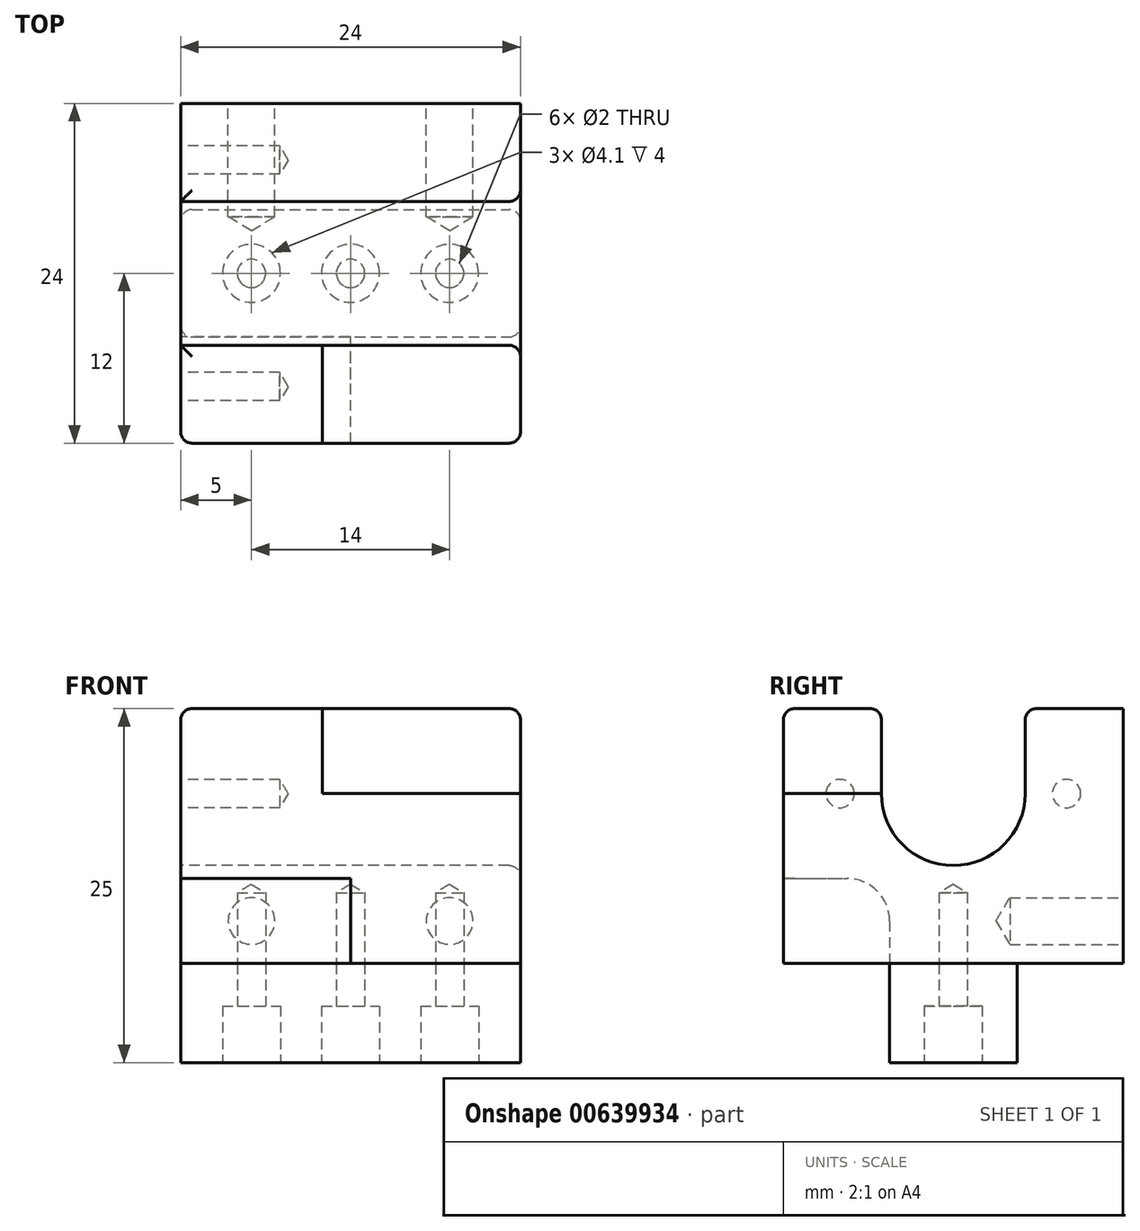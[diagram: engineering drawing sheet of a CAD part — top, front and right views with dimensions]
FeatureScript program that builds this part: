
annotation { "Feature Type Name" : "Feature", "Feature Type Description" : "" }
export const myFeature = defineFeature(function(context is Context, id is Id, definition is map)
    precondition{}
    {
        {
            var Q0;
            Q0=qCreatedBy(makeId("Right.planeOp"),FACE);
            var sketch = newSketch(context, id + "F0", { "sketchPlane" : qUnion([Q0])});
            skLineSegment(sketch, "E0.bottom", {"start": v(0, 0) * mm, "end": v(24, 0) * mm});
            skLineSegment(sketch, "E0.top", {"start": v(0, 18) * mm, "end": v(24, 18) * mm});
            skLineSegment(sketch, "E0.left", {"start": v(0, 0) * mm, "end": v(0, 18) * mm});
            skLineSegment(sketch, "E0.right", {"start": v(24, 0) * mm, "end": v(24, 18) * mm});
            skCircle(sketch, "E1", {"center": v(12, 12) * mm, "radius": 5.08 * mm});
            skLineSegment(sketch, "E2", {"start": v(12, 18) * mm, "end": v(12, 0) * mm, "construction": true});
            skLineSegment(sketch, "E3.bottom", {"start": v(17.08, 12) * mm, "end": v(6.92, 12) * mm});
            skLineSegment(sketch, "E3.top", {"start": v(17.08, 18) * mm, "end": v(6.92, 18) * mm});
            skLineSegment(sketch, "E3.left", {"start": v(17.08, 12) * mm, "end": v(17.08, 18) * mm});
            skLineSegment(sketch, "E3.right", {"start": v(6.92, 12) * mm, "end": v(6.92, 18) * mm});
            skSolve(sketch);
        }
        {
            var Q0;
            Q0=makeQuery(id+"F0.imprint","IMPRINT",FACE,{"disambiguationData":[TD([[makeQuery(id+"F0.imprint","IMPRINT",EDGE,{"derivedFrom":sQuery(id+"F0.wireOp",EDGE,"E0.bottom")}),1.0]])]});
            extrude(context, id + "F1", {"entities" : qUnion([Q0]), "depth" : 24 * mm, "offsetDistance" : 25 * mm});
        }
        {
            var Q0;
            Q0=makeQuery(id+"F1.opExtrude","CAP_FACE",FACE,{"disambiguationData":[OSD([sQuery(id+"F0.wireOp",EDGE,"E0.bottom"),sQuery(id+"F0.wireOp",EDGE,"E0.top"),sQuery(id+"F0.wireOp",EDGE,"E0.left"),sQuery(id+"F0.wireOp",EDGE,"E0.right"),sQuery(id+"F0.wireOp",EDGE,"E1"),sQuery(id+"F0.wireOp",EDGE,"E3.left"),sQuery(id+"F0.wireOp",EDGE,"E3.right")])],"isStart":true});
            var sketch = newSketch(context, id + "F2", { "sketchPlane" : qUnion([Q0])});
            skLineSegment(sketch, "E4", {"start": v(-20, 12) * mm, "end": v(-4, 12) * mm, "construction": true});
            skPoint(sketch, "E5", {"position": v(-20, 12) * mm});
            skPoint(sketch, "E6", {"position": v(-4, 12) * mm});
            skSolve(sketch);
        }
        {
            var Q0;
            Q0=sQuery(id+"F2.wireOp",VERTEX,"E5");
            var Q1;
            Q1=sQuery(id+"F2.wireOp",VERTEX,"E6");
            var Q2;
            Q2=makeQuery(id+"F1.opExtrude","SWEPT_BODY",BODY,{"disambiguationData":[OSD([sQuery(id+"F0.wireOp",EDGE,"E0.bottom"),sQuery(id+"F0.wireOp",EDGE,"E0.top"),sQuery(id+"F0.wireOp",EDGE,"E0.left"),sQuery(id+"F0.wireOp",EDGE,"E0.right"),sQuery(id+"F0.wireOp",EDGE,"E1"),sQuery(id+"F0.wireOp",EDGE,"E3.left"),sQuery(id+"F0.wireOp",EDGE,"E3.right")])]});
            hole(context, id + "F3", {"style" : HoleStyle.SIMPLE, "endStyle" : HoleEndStyle.BLIND, "holeDiameter" : 2 * mm, "majorDiameter" : 5 * mm, "holeDepth" : 7 * mm, "isTappedThrough" : true, "tappedDepth" : 7 * mm, "tapClearance" : 2, "startFromSketch" : true, "locations" : qUnion([Q0, Q1]), "scope" : qUnion([Q2])});
        }
        {
            var Q0;
            Q0=makeQuery(id+"F1.opExtrude","SWEPT_FACE",FACE,{"disambiguationData":[OSD([sQuery(id+"F0.wireOp",EDGE,"E0.right")])]});
            var sketch = newSketch(context, id + "F4", { "sketchPlane" : qUnion([Q0])});
            skLineSegment(sketch, "E7", {"start": v(0, 3) * mm, "end": v(-26.79, 3) * mm, "construction": true});
            skPoint(sketch, "E8", {"position": v(-19, 3) * mm});
            skPoint(sketch, "E9", {"position": v(-5, 3) * mm});
            skSolve(sketch);
        }
        {
            var Q0;
            Q0=sQuery(id+"F4.wireOp",VERTEX,"E8");
            var Q1;
            Q1=sQuery(id+"F4.wireOp",VERTEX,"E9");
            var Q2;
            Q2=makeQuery(id+"F1.opExtrude","SWEPT_BODY",BODY,{"disambiguationData":[OSD([sQuery(id+"F0.wireOp",EDGE,"E0.bottom"),sQuery(id+"F0.wireOp",EDGE,"E0.top"),sQuery(id+"F0.wireOp",EDGE,"E0.left"),sQuery(id+"F0.wireOp",EDGE,"E0.right"),sQuery(id+"F0.wireOp",EDGE,"E1"),sQuery(id+"F0.wireOp",EDGE,"E3.left"),sQuery(id+"F0.wireOp",EDGE,"E3.right")])]});
            hole(context, id + "F5", {"style" : HoleStyle.SIMPLE, "endStyle" : HoleEndStyle.BLIND, "standardTappedOrClearance" : lookupTablePath({ "standard" : "ISO", "fit" : "Normal", "size" : "M3", "type" : "Clearance" }), "standardBlindInLast" : lookupTablePath({ "fit" : "Standard", "standard" : "ISO", "size" : "M3", "type" : "Clearance" }), "holeDiameter" : 3.3 * mm, "majorDiameter" : 5 * mm, "holeDepth" : 8 * mm, "isTappedThrough" : true, "tappedDepth" : 7 * mm, "tapClearance" : 2, "startFromSketch" : true, "locations" : qUnion([Q0, Q1]), "scope" : qUnion([Q2])});
        }
        {
            var Q0;
            Q0=makeQuery(id+"F1.opExtrude","SWEPT_FACE",FACE,{"disambiguationData":[OSD([sQuery(id+"F0.wireOp",EDGE,"E0.bottom")])]});
            var sketch = newSketch(context, id + "F6", { "sketchPlane" : qUnion([Q0])});
            skLineSegment(sketch, "E10.bottom", {"start": v(0, -7.5) * mm, "end": v(24, -7.5) * mm});
            skLineSegment(sketch, "E10.top", {"start": v(0, -16.5) * mm, "end": v(24, -16.5) * mm});
            skLineSegment(sketch, "E10.left", {"start": v(0, -7.5) * mm, "end": v(0, -16.5) * mm});
            skLineSegment(sketch, "E10.right", {"start": v(24, -7.5) * mm, "end": v(24, -16.5) * mm});
            skSolve(sketch);
        }
        {
            var Q0;
            Q0 = qSketchRegion(id + "F6", true);
            extrude(context, id + "F7", {"entities" : qUnion([Q0]), "depth" : 7 * mm, "offsetDistance" : 25 * mm});
        }
        {
            var Q0;
            Q0=makeQuery(id+"F7.opExtrude","CAP_FACE",FACE,{"disambiguationData":[OSD([sQuery(id+"F6.wireOp",EDGE,"E10.bottom"),sQuery(id+"F6.wireOp",EDGE,"E10.top"),sQuery(id+"F6.wireOp",EDGE,"E10.left"),sQuery(id+"F6.wireOp",EDGE,"E10.right")])],"isStart":false});
            var sketch = newSketch(context, id + "F8", { "sketchPlane" : qUnion([Q0])});
            skLineSegment(sketch, "E11", {"start": v(24, -12) * mm, "end": v(0, -12) * mm, "construction": true});
            skPoint(sketch, "E12", {"position": v(12, -12) * mm});
            skPoint(sketch, "E13", {"position": v(19, -12) * mm});
            skPoint(sketch, "E14", {"position": v(5, -12) * mm});
            skSolve(sketch);
        }
        {
            var Q0;
            Q0=sQuery(id+"F8.wireOp",VERTEX,"E14");
            var Q1;
            Q1=sQuery(id+"F8.wireOp",VERTEX,"E12");
            var Q2;
            Q2=sQuery(id+"F8.wireOp",VERTEX,"E13");
            var Q3;
            Q3=makeQuery(id+"F1.opExtrude","SWEPT_BODY",BODY,{"disambiguationData":[OSD([sQuery(id+"F0.wireOp",EDGE,"E0.bottom"),sQuery(id+"F0.wireOp",EDGE,"E0.top"),sQuery(id+"F0.wireOp",EDGE,"E0.left"),sQuery(id+"F0.wireOp",EDGE,"E0.right"),sQuery(id+"F0.wireOp",EDGE,"E1"),sQuery(id+"F0.wireOp",EDGE,"E3.left"),sQuery(id+"F0.wireOp",EDGE,"E3.right")])]});
            var Q4;
            Q4=makeQuery(id+"F7.opExtrude","SWEPT_BODY",BODY,{"disambiguationData":[OSD([sQuery(id+"F6.wireOp",EDGE,"E10.bottom"),sQuery(id+"F6.wireOp",EDGE,"E10.top"),sQuery(id+"F6.wireOp",EDGE,"E10.left"),sQuery(id+"F6.wireOp",EDGE,"E10.right")])]});
            hole(context, id + "F9", {"style" : HoleStyle.C_BORE, "endStyle" : HoleEndStyle.BLIND, "holeDiameter" : 2 * mm, "cBoreDiameter" : 4.1 * mm, "cBoreDepth" : 4 * mm, "majorDiameter" : 5 * mm, "holeDepth" : 12 * mm, "isTappedThrough" : true, "tappedDepth" : 7 * mm, "tapClearance" : 2, "startFromSketch" : true, "locations" : qUnion([Q0, Q1, Q2]), "scope" : qUnion([Q3, Q4])});
        }
        {
            var Q0;
            Q0=makeQuery(id+"F1.opExtrude","CAP_FACE",FACE,{"disambiguationData":[OSD([sQuery(id+"F0.wireOp",EDGE,"E0.bottom"),sQuery(id+"F0.wireOp",EDGE,"E0.top"),sQuery(id+"F0.wireOp",EDGE,"E0.left"),sQuery(id+"F0.wireOp",EDGE,"E0.right"),sQuery(id+"F0.wireOp",EDGE,"E1"),sQuery(id+"F0.wireOp",EDGE,"E3.left"),sQuery(id+"F0.wireOp",EDGE,"E3.right")])],"isStart":true});
            var sketch = newSketch(context, id + "F10", { "sketchPlane" : qUnion([Q0])});
            skCircle(sketch, "E15", {"center": v(-4.5, 3) * mm, "radius": 3 * mm});
            skLineSegment(sketch, "E16", {"start": v(-7.5, 3) * mm, "end": v(-7.5, 0) * mm});
            skLineSegment(sketch, "E17", {"start": v(-7.5, 0) * mm, "end": v(0, 0) * mm});
            skLineSegment(sketch, "E18", {"start": v(0, 0) * mm, "end": v(0, 6) * mm});
            skLineSegment(sketch, "E19", {"start": v(0, 6) * mm, "end": v(-4.5, 6) * mm});
            skSolve(sketch);
        }
        {
            var Q0;
            Q0 = qSketchRegion(id + "F10", true);
            extrude(context, id + "F11", {"entities" : qUnion([Q0]), "operationType" : NewBodyOperationType.REMOVE, "oppositeDirection" : true, "depth" : 12 * mm, "offsetDistance" : 25 * mm});
        }
        {
            var Q0;
            Q0=makeQuery(id+"F1.opExtrude","CAP_FACE",FACE,{"disambiguationData":[OSD([sQuery(id+"F0.wireOp",EDGE,"E0.bottom"),sQuery(id+"F0.wireOp",EDGE,"E0.top"),sQuery(id+"F0.wireOp",EDGE,"E0.left"),sQuery(id+"F0.wireOp",EDGE,"E0.right"),sQuery(id+"F0.wireOp",EDGE,"E1"),sQuery(id+"F0.wireOp",EDGE,"E3.left"),sQuery(id+"F0.wireOp",EDGE,"E3.right")])],"isStart":false});
            var sketch = newSketch(context, id + "F12", { "sketchPlane" : qUnion([Q0])});
            skLineSegment(sketch, "E20.bottom", {"start": v(0, 18) * mm, "end": v(6.92, 18) * mm});
            skLineSegment(sketch, "E20.top", {"start": v(0, 12) * mm, "end": v(6.92, 12) * mm});
            skLineSegment(sketch, "E20.left", {"start": v(0, 18) * mm, "end": v(0, 12) * mm});
            skLineSegment(sketch, "E20.right", {"start": v(6.92, 18) * mm, "end": v(6.92, 12) * mm});
            skSolve(sketch);
        }
        {
            var Q0;
            Q0 = qSketchRegion(id + "F12", true);
            extrude(context, id + "F13", {"entities" : qUnion([Q0]), "operationType" : NewBodyOperationType.REMOVE, "oppositeDirection" : true, "depth" : 14 * mm, "offsetDistance" : 25 * mm});
        }
        {
            var Q0;
            Q0=makeQuery(id+"F1.opExtrude","CAP_EDGE",EDGE,{"disambiguationData":[OSD([sQuery(id+"F0.wireOp",EDGE,"E0.left")])],"isStart":true});
            var Q1;
            Q1=makeQuery(id+"F11.boolean.opBoolean","COPY",EDGE,{"derivedFrom":makeQuery(id+"F11.opExtrude","CAP_EDGE",EDGE,{"disambiguationData":[OSD([sQuery(id+"F10.wireOp",EDGE,"E19")])],"isStart":true})});
            var Q2;
            Q2=makeQuery(id+"F11.boolean.opBoolean","COPY",EDGE,{"derivedFrom":makeQuery(id+"F11.opExtrude","SWEPT_EDGE",EDGE,{"disambiguationData":[OSD([sQuery(id+"F0.wireOp",EDGE,"E0.left"),sQuery(id+"F10.wireOp",EDGE,"E18"),sQuery(id+"F10.wireOp",EDGE,"E19")])]})});
            var Q3;
            Q3=makeQuery(id+"F7.opExtrude","SWEPT_EDGE",EDGE,{"disambiguationData":[OSD([sQuery(id+"F0.wireOp",EDGE,"E0.bottom"),sQuery(id+"F6.wireOp",EDGE,"E10.bottom"),sQuery(id+"F6.wireOp",EDGE,"E10.left")])]});
            var Q4;
            Q4=makeQuery(id+"F7.opExtrude","SWEPT_EDGE",EDGE,{"disambiguationData":[OSD([sQuery(id+"F0.wireOp",EDGE,"E0.bottom"),sQuery(id+"F6.wireOp",EDGE,"E10.top"),sQuery(id+"F6.wireOp",EDGE,"E10.left")])]});
            var Q5;
            Q5=makeQuery(id+"F7.opExtrude","SWEPT_EDGE",EDGE,{"disambiguationData":[OSD([sQuery(id+"F0.wireOp",EDGE,"E0.bottom"),sQuery(id+"F6.wireOp",EDGE,"E10.top"),sQuery(id+"F6.wireOp",EDGE,"E10.right")])]});
            var Q6;
            Q6=makeQuery(id+"F7.opExtrude","SWEPT_EDGE",EDGE,{"disambiguationData":[OSD([sQuery(id+"F0.wireOp",EDGE,"E0.bottom"),sQuery(id+"F6.wireOp",EDGE,"E10.bottom"),sQuery(id+"F6.wireOp",EDGE,"E10.right")])]});
            var Q7;
            Q7=makeQuery(id+"F11.boolean.opBoolean","COPY",EDGE,{"derivedFrom":makeQuery(id+"F11.opExtrude","CAP_EDGE",EDGE,{"disambiguationData":[OSD([sQuery(id+"F10.wireOp",EDGE,"E18")])],"isStart":false})});
            var Q8;
            Q8=makeQuery(id+"F1.opExtrude","CAP_EDGE",EDGE,{"disambiguationData":[OSD([sQuery(id+"F0.wireOp",EDGE,"E0.left")])],"isStart":false});
            var Q9;
            Q9=makeQuery(id+"F13.boolean.opBoolean","COPY",EDGE,{"derivedFrom":makeQuery(id+"F13.opExtrude","SWEPT_EDGE",EDGE,{"disambiguationData":[OSD([sQuery(id+"F0.wireOp",EDGE,"E0.left"),sQuery(id+"F12.wireOp",EDGE,"E20.top"),sQuery(id+"F12.wireOp",EDGE,"E20.left")])]})});
            var Q10;
            Q10=makeQuery(id+"F13.boolean.opBoolean","COPY",EDGE,{"derivedFrom":makeQuery(id+"F13.opExtrude","CAP_EDGE",EDGE,{"disambiguationData":[OSD([sQuery(id+"F12.wireOp",EDGE,"E20.top")])],"isStart":true})});
            var Q11;
            Q11=makeQuery(id+"F13.boolean.opBoolean","COPY",EDGE,{"derivedFrom":makeQuery(id+"F13.opExtrude","CAP_EDGE",EDGE,{"disambiguationData":[OSD([sQuery(id+"F12.wireOp",EDGE,"E20.left")])],"isStart":false})});
            var Q12;
            Q12=makeQuery(id+"F1.opExtrude","CAP_EDGE",EDGE,{"disambiguationData":[OSD([sQuery(id+"F0.wireOp",EDGE,"E1")])],"isStart":false});
            var Q13;
            Q13=makeQuery(id+"F1.opExtrude","SWEPT_EDGE",EDGE,{"disambiguationData":[OSD([sQuery(id+"F0.wireOp",EDGE,"E0.top"),sQuery(id+"F0.wireOp",EDGE,"E0.left")])]});
            var Q14;
            {var subQ0=sQuery(id+"F0.wireOp",EDGE,"E0.top");Q14=makeQuery(id+"F1.opExtrude","CAP_EDGE",EDGE,{"disambiguationData":[OSD([subQ0]),TDD([makeQuery(id+"F0.imprint","IMPRINT",EDGE,{"disambiguationData":[TD([[makeQuery(id+"F0.imprint","INTERSECT",VERTEX,{"derivedFrom":[subQ0,sQuery(id+"F0.wireOp",EDGE,"E0.left")]}),-1.0]])],"derivedFrom":subQ0})])],"isStart":true});}
            var Q15;
            Q15=makeQuery(id+"F1.opExtrude","SWEPT_EDGE",EDGE,{"disambiguationData":[OSD([sQuery(id+"F0.wireOp",EDGE,"E0.top"),sQuery(id+"F0.wireOp",EDGE,"E3.top"),sQuery(id+"F0.wireOp",EDGE,"E3.right")])]});
            var Q16;
            Q16=makeQuery(id+"F13.boolean.opBoolean","COPY",EDGE,{"derivedFrom":makeQuery(id+"F13.opExtrude","CAP_EDGE",EDGE,{"disambiguationData":[OSD([sQuery(id+"F12.wireOp",EDGE,"E20.bottom")])],"isStart":false})});
            var Q17;
            Q17=makeQuery(id+"F1.opExtrude","SWEPT_EDGE",EDGE,{"disambiguationData":[OSD([sQuery(id+"F0.wireOp",EDGE,"E0.top"),sQuery(id+"F0.wireOp",EDGE,"E3.top"),sQuery(id+"F0.wireOp",EDGE,"E3.left")])]});
            var Q18;
            {var subQ0=sQuery(id+"F0.wireOp",EDGE,"E0.top");Q18=makeQuery(id+"F1.opExtrude","CAP_EDGE",EDGE,{"disambiguationData":[OSD([subQ0]),TDD([makeQuery(id+"F0.imprint","IMPRINT",EDGE,{"disambiguationData":[TD([[makeQuery(id+"F0.imprint","INTERSECT",VERTEX,{"derivedFrom":[subQ0,sQuery(id+"F0.wireOp",EDGE,"E0.right")]}),1.0]])],"derivedFrom":subQ0})])],"isStart":true});}
            var Q19;
            {var subQ0=sQuery(id+"F0.wireOp",EDGE,"E0.top");Q19=makeQuery(id+"F1.opExtrude","CAP_EDGE",EDGE,{"disambiguationData":[OSD([subQ0]),TDD([makeQuery(id+"F0.imprint","IMPRINT",EDGE,{"disambiguationData":[TD([[makeQuery(id+"F0.imprint","INTERSECT",VERTEX,{"derivedFrom":[subQ0,sQuery(id+"F0.wireOp",EDGE,"E0.right")]}),1.0]])],"derivedFrom":subQ0})])],"isStart":false});}
            fillet(context, id + "F14", {"entities" : qUnion([Q0, Q1, Q2, Q3, Q4, Q5, Q6, Q7, Q8, Q9, Q10, Q11, Q12, Q13, Q14, Q15, Q16, Q17, Q18, Q19]), "radius" : 0.8 * mm, "tangentPropagation" : true, "allowEdgeOverflow" : false});
        }
    });
